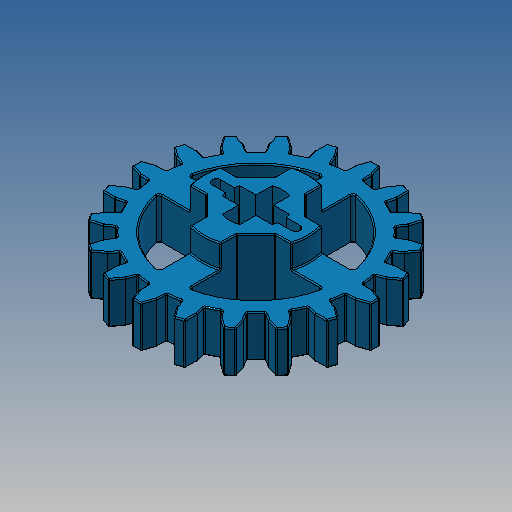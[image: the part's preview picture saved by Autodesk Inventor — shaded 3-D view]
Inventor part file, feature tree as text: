
AUTODESK INVENTOR PART (.ipt)
format: ipt  version: 2025 (Build 290162010, 162A)  size: 1,227,776 bytes
history: native  units: in
note: dims shown in document units (in); Inventor stores cm internally (conversion verified against a paired STEP export)
features: extrude x3, fillet x3, sketch x1, pattern_circular x1
ambient origin geometry x8: Origin, YZ Plane, XZ Plane, XY Plane, X Axis, Y Axis, Z Axis, Center Point
bodies: Solid1 (feature_tree)
feature tree (8):
  sketch  "Sketch2"  dims[d1=0.189in d2=0.063in d3=0.0315in d4=0.2835in d6=135.0deg d7=0.1102in d8=0.252in d9=0.378in d10=0.4264in d11=0.0315in d12=0.0591in d13=0.063in d14=0.0413in d15=0.1496in d16=0.0in d17=0.315in d18=0.0in d19=0.1496in d20=0.0in d21=0.0039in d22=7.874in d23=360.0deg d25=0.0039in d26=0.0in d27=0.0in d28=0.0in d30=0.0734in d31=0.0551in d32=0.0079in]
  extrude  "Extrusion1"  Depth=0.0079in
  extrude  "Extrusion2"  Depth=0.0079in
  extrude  "Extrusion3"  Depth=0.0079in
  fillet  "Fillet1"  [1 undecoded]
  pattern_circular  "Circular Pattern1"  [2 undecoded]
  fillet  "Rundung3"  Radius=0.252in
  fillet  "Fillet2"  Radius=0.378in
note: 3 required parameter values undecoded (feature->parameter linkage not recoverable at this tier; creation-order binding heuristic only, values carry confidence <= 0.55)
